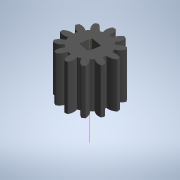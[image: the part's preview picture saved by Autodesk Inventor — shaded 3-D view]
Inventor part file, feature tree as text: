
AUTODESK INVENTOR PART (.ipt)
format: ipt  version: 2020 (Build 240168000, 168)  size: 160,256 bytes
history: native  units: mm (DEFAULTED — no unit token found)
features: other x3, plane x2, imported_body x1
ambient origin geometry x8: Origin, YZ Plane, XZ Plane, XY Plane, X Axis, Y Axis, Z Axis, Center Point
bodies: Body1 (feature_tree)
feature tree (6):
  other  "Gear HS 12 tooth"
  parser-record x1  (decoder bookkeeping rows leaked as tree rows — omitted from the tree; the rows remain in map.json)
  other  "Work Axis1"
  imported_body  "Base1"
  plane  "Work Plane1"
  plane  "Work Plane2"
